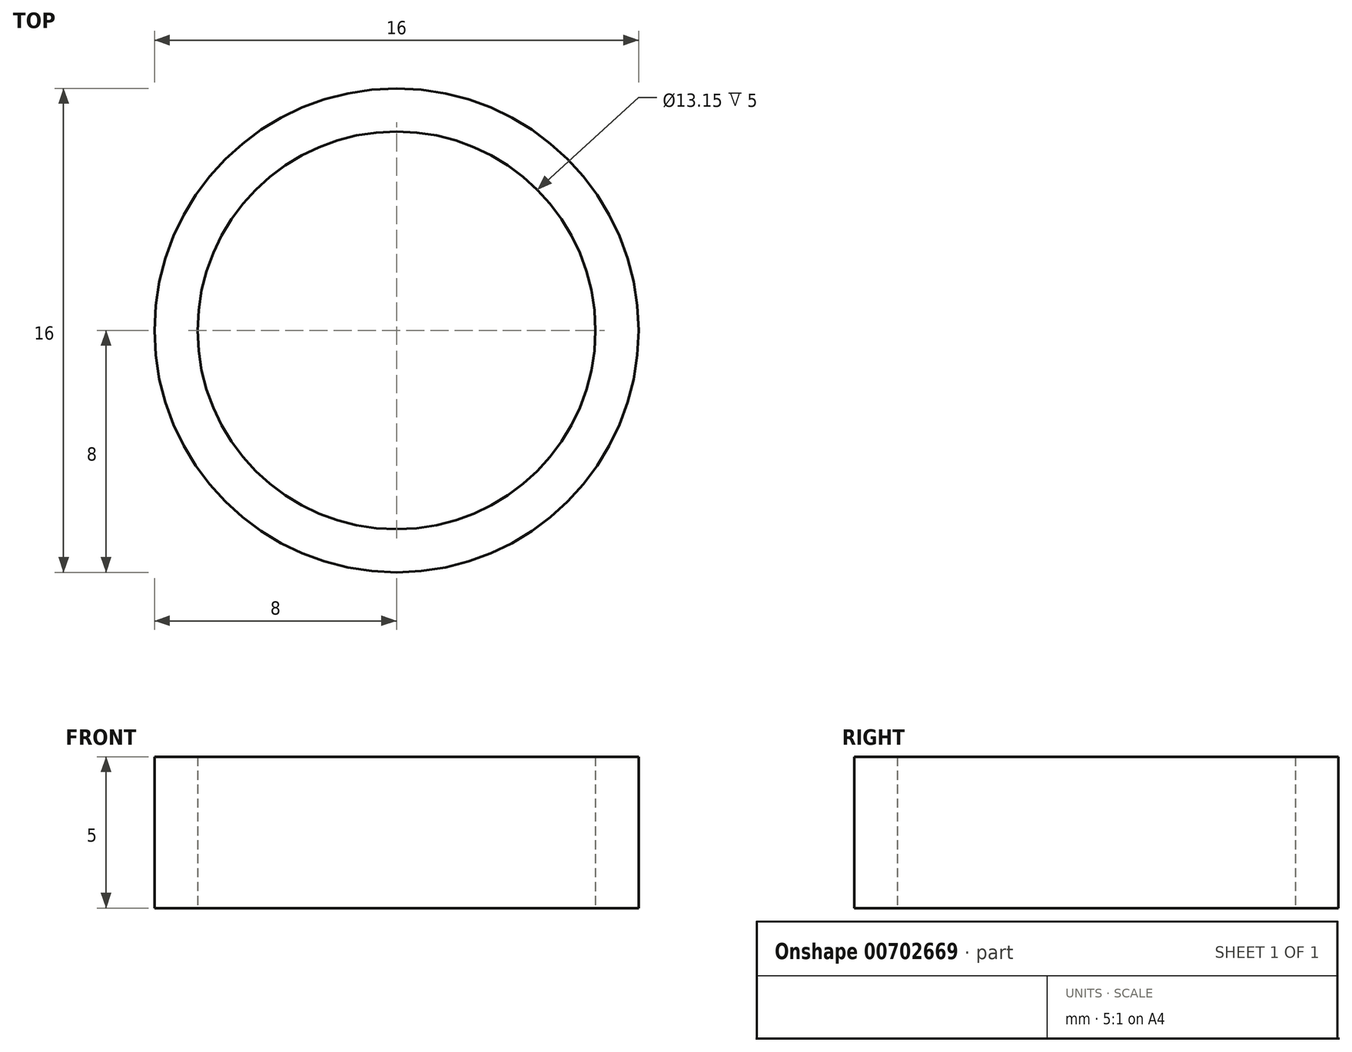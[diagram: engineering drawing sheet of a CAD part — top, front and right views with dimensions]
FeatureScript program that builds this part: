
annotation { "Feature Type Name" : "Feature", "Feature Type Description" : "" }
export const myFeature = defineFeature(function(context is Context, id is Id, definition is map)
    precondition{}
    {
        {
            var Q0;
            Q0=qCreatedBy(makeId("Top.planeOp"),FACE);
            var sketch = newSketch(context, id + "F0", { "sketchPlane" : qUnion([Q0])});
            skCircle(sketch, "E0", {"center": v(0, 0) * mm, "radius": 8 * mm});
            skCircle(sketch, "E1", {"center": v(0, 0) * mm, "radius": 6.58 * mm});
            skSolve(sketch);
        }
        {
            var Q0;
            Q0=makeQuery(id+"F0.imprint","IMPRINT",FACE,{"disambiguationData":[TD([[makeQuery(id+"F0.imprint","IMPRINT",EDGE,{"derivedFrom":sQuery(id+"F0.wireOp",EDGE,"E0")}),1.0]])]});
            extrude(context, id + "F1", {"entities" : qUnion([Q0]), "depth" : 5 * mm, "offsetDistance" : 25 * mm});
        }
    });
